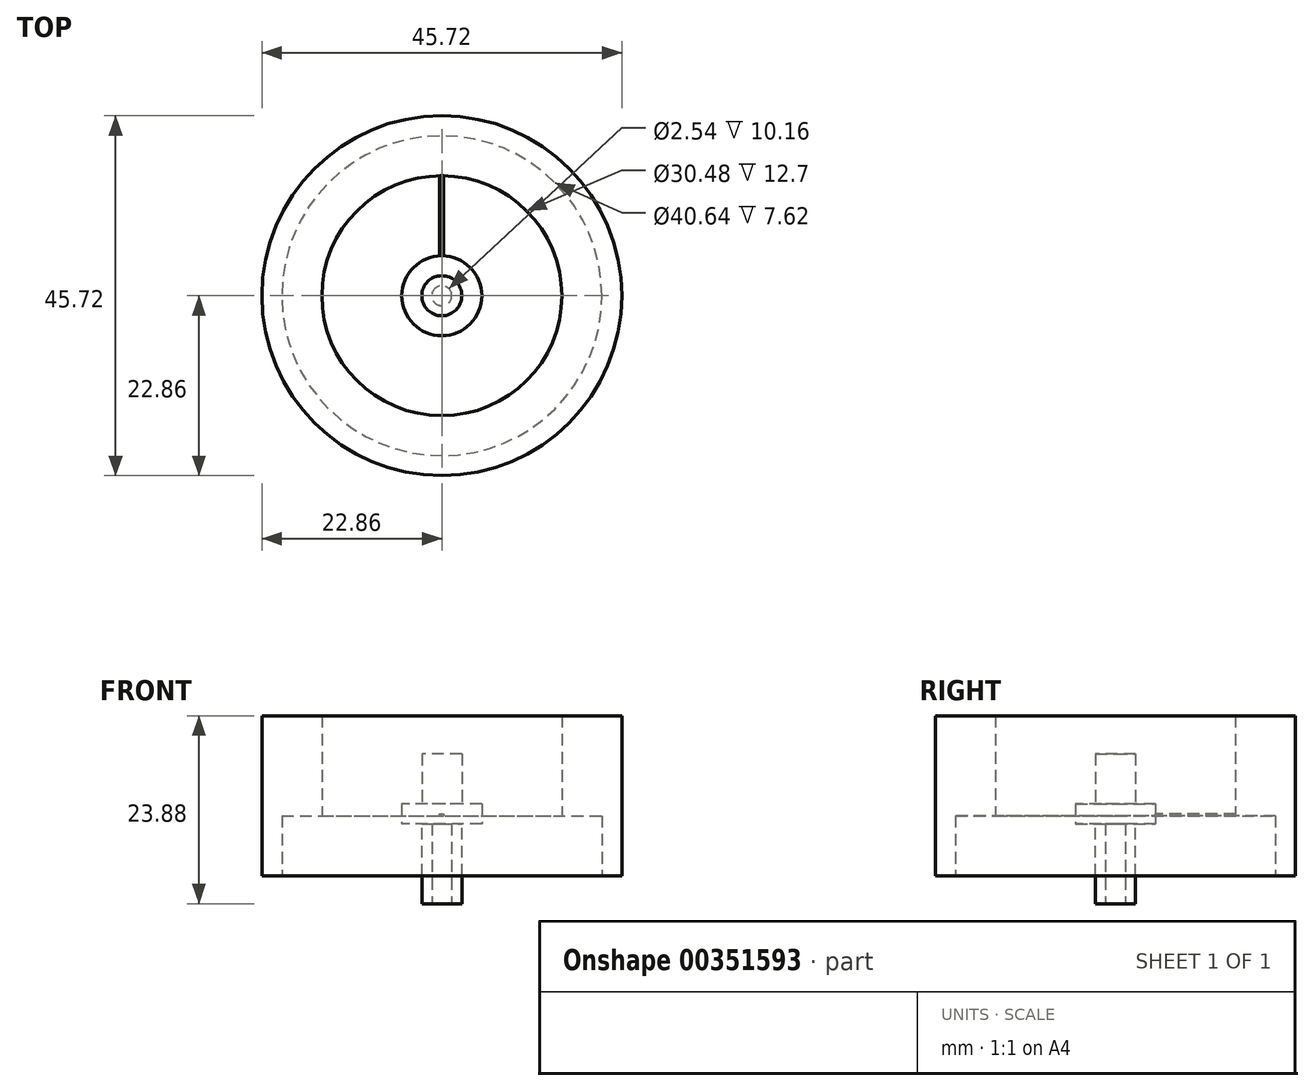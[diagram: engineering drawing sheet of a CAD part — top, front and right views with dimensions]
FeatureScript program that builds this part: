
annotation { "Feature Type Name" : "Feature", "Feature Type Description" : "" }
export const myFeature = defineFeature(function(context is Context, id is Id, definition is map)
    precondition{}
    {
        {
            var Q0;
            Q0=qCreatedBy(makeId("Top.planeOp"),FACE);
            var sketch = newSketch(context, id + "F0", { "sketchPlane" : qUnion([Q0])});
            skCircle(sketch, "E0", {"center": v(0, 0) * mm, "radius": 5.08 * mm});
            skSolve(sketch);
        }
        {
            var Q0;
            Q0 = qSketchRegion(id + "F0", true);
            extrude(context, id + "F1", {"entities" : qUnion([Q0]), "depth" : 2.54 * mm, "symmetric" : true});
        }
        {
            var Q0;
            Q0=qCreatedBy(makeId("Top.planeOp"),FACE);
            var sketch = newSketch(context, id + "F2", { "sketchPlane" : qUnion([Q0])});
            skCircle(sketch, "E1", {"center": v(0, 0) * mm, "radius": 2.54 * mm});
            skSolve(sketch);
        }
        {
            var Q0;
            Q0 = qSketchRegion(id + "F2", true);
            extrude(context, id + "F3", {"entities" : qUnion([Q0]), "operationType" : NewBodyOperationType.ADD, "depth" : 7.62 * mm});
        }
        {
            var Q0;
            Q0=makeQuery(id+"F1.opExtrude","CAP_FACE",FACE,{"disambiguationData":[OSD([sQuery(id+"F0.wireOp",EDGE,"E0")])],"isStart":true});
            var sketch = newSketch(context, id + "F4", { "sketchPlane" : qUnion([Q0])});
            skCircle(sketch, "E2", {"center": v(0, 0) * mm, "radius": 2.54 * mm});
            skSolve(sketch);
        }
        {
            var Q0;
            Q0 = qSketchRegion(id + "F4", true);
            extrude(context, id + "F5", {"entities" : qUnion([Q0]), "operationType" : NewBodyOperationType.ADD, "depth" : 10.16 * mm});
        }
        {
            var Q0;
            Q0=makeQuery(id+"F5.opExtrude","CAP_FACE",FACE,{"disambiguationData":[OSD([sQuery(id+"F4.wireOp",EDGE,"E2")])],"isStart":false});
            var sketch = newSketch(context, id + "F6", { "sketchPlane" : qUnion([Q0])});
            skCircle(sketch, "E3", {"center": v(0, 0) * mm, "radius": 1.27 * mm});
            skSolve(sketch);
        }
        {
            var Q0;
            Q0 = qSketchRegion(id + "F6", true);
            extrude(context, id + "F7", {"entities" : qUnion([Q0]), "operationType" : NewBodyOperationType.REMOVE, "oppositeDirection" : true, "depth" : 10.16 * mm});
        }
        {
            var Q0;
            Q0=qCreatedBy(makeId("Front.planeOp"),FACE);
            cPlane(context, id + "F8", {"entities" : qUnion([Q0]), "cplaneType" : CPlaneType.OFFSET, "offset" : 5.08 * mm, "oppositeDirection" : true, "width" : 152.4 * mm, "height" : 152.4 * mm});
        }
        {
            var Q0;
            Q0=qCreatedBy(id+"F8.planeOp",FACE);
            var sketch = newSketch(context, id + "F9", { "sketchPlane" : qUnion([Q0])});
            skPoint(sketch, "E4.0", {"position": v(-0.26, -0.25) * mm});
            skPoint(sketch, "E5.0", {"position": v(0.25, 0) * mm});
            skLineSegment(sketch, "E6.bottom", {"start": v(-0.26, -0.25) * mm, "end": v(0.25, -0.25) * mm});
            skLineSegment(sketch, "E6.top", {"start": v(-0.26, 0) * mm, "end": v(0.25, 0) * mm});
            skLineSegment(sketch, "E6.left", {"start": v(-0.26, -0.25) * mm, "end": v(-0.26, 0) * mm});
            skLineSegment(sketch, "E6.right", {"start": v(0.25, -0.25) * mm, "end": v(0.25, 0) * mm});
            skPoint(sketch, "E7", {"position": v(-0.26, 0) * mm});
            skPoint(sketch, "E8", {"position": v(0.25, -0.25) * mm});
            skSolve(sketch);
        }
        {
            var Q0;
            Q0 = qSketchRegion(id + "F9", true);
            extrude(context, id + "F10", {"entities" : qUnion([Q0]), "operationType" : NewBodyOperationType.ADD, "oppositeDirection" : true, "depth" : 10.16 * mm});
        }
        {
            var Q0;
            Q0=makeQuery(id+"F10.opExtrude","SWEPT_FACE",FACE,{"disambiguationData":[OSD([sQuery(id+"F9.wireOp",EDGE,"E6.right")])]});
            cPlane(context, id + "F11", {"entities" : qUnion([Q0]), "cplaneType" : CPlaneType.OFFSET, "offset" : 0 * mm, "width" : 152.4 * mm, "height" : 152.4 * mm});
        }
        {
            var Q0;
            Q0=qCreatedBy(id+"F11.planeOp",FACE);
            var sketch = newSketch(context, id + "F12", { "sketchPlane" : qUnion([Q0])});
            skPoint(sketch, "E9.0", {"position": v(15.24, -0.25) * mm});
            skLineSegment(sketch, "E10.bottom", {"start": v(15.24, -0.25) * mm, "end": v(22.86, -0.25) * mm});
            skLineSegment(sketch, "E10.top", {"start": v(15.24, 12.45) * mm, "end": v(22.86, 12.45) * mm});
            skLineSegment(sketch, "E10.left", {"start": v(15.24, -0.25) * mm, "end": v(15.24, 12.45) * mm});
            skLineSegment(sketch, "E10.right", {"start": v(22.86, -0.25) * mm, "end": v(22.86, 12.45) * mm});
            skSolve(sketch);
        }
        {
            var Q0;
            Q0 = qSketchRegion(id + "F12", true);
            var Q1;
            Q1=makeQuery(id+"F1.opExtrude","CAP_EDGE",EDGE,{"disambiguationData":[OSD([sQuery(id+"F0.wireOp",EDGE,"E0")])],"isStart":false});
            revolve(context, id + "F13", {"operationType" : NewBodyOperationType.ADD, "entities" : qUnion([Q0]), "axis" : qUnion([Q1]), "revolveType" : RevolveType.FULL});
        }
        {
            var Q0;
            Q0=qCreatedBy(id+"F11.planeOp",FACE);
            var sketch = newSketch(context, id + "F14", { "sketchPlane" : qUnion([Q0])});
            skPoint(sketch, "E11.0", {"position": v(22.86, -0.25) * mm});
            skLineSegment(sketch, "E12.bottom", {"start": v(22.86, -0.25) * mm, "end": v(20.32, -0.25) * mm});
            skLineSegment(sketch, "E12.top", {"start": v(22.86, -7.87) * mm, "end": v(20.32, -7.87) * mm});
            skLineSegment(sketch, "E12.left", {"start": v(22.86, -0.25) * mm, "end": v(22.86, -7.87) * mm});
            skLineSegment(sketch, "E12.right", {"start": v(20.32, -0.25) * mm, "end": v(20.32, -7.87) * mm});
            skSolve(sketch);
        }
        {
            var Q0;
            Q0 = qSketchRegion(id + "F14", true);
            var Q1;
            Q1=makeQuery(id+"F1.opExtrude","CAP_EDGE",EDGE,{"disambiguationData":[OSD([sQuery(id+"F0.wireOp",EDGE,"E0")])],"isStart":false});
            revolve(context, id + "F15", {"operationType" : NewBodyOperationType.ADD, "entities" : qUnion([Q0]), "axis" : qUnion([Q1]), "revolveType" : RevolveType.FULL});
        }
    });
